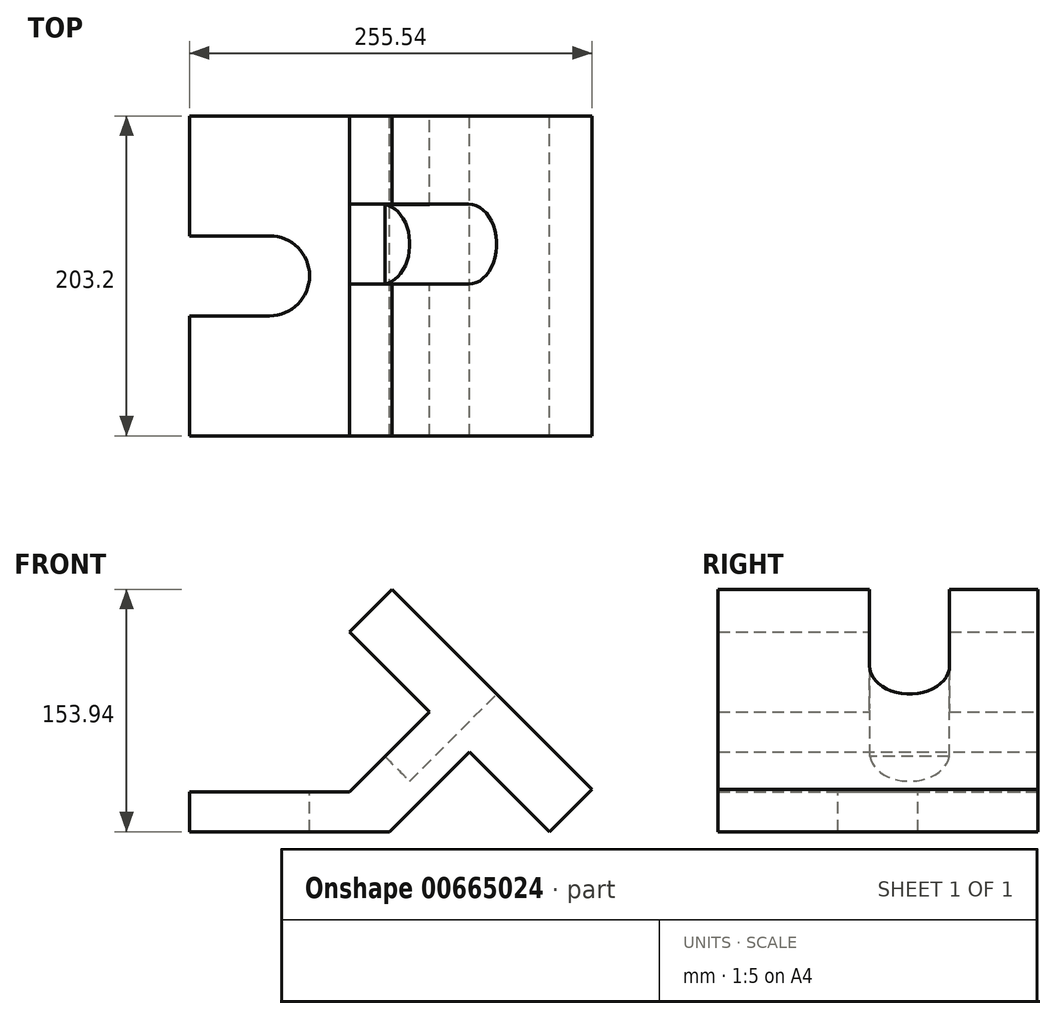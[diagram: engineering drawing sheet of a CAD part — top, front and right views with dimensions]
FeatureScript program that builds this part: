
annotation { "Feature Type Name" : "Feature", "Feature Type Description" : "" }
export const myFeature = defineFeature(function(context is Context, id is Id, definition is map)
    precondition{}
    {
        {
            var Q0;
            Q0=qCreatedBy(makeId("Front.planeOp"),FACE);
            var sketch = newSketch(context, id + "F0", { "sketchPlane" : qUnion([Q0])});
            skLineSegment(sketch, "E0", {"start": v(0, 0) * mm, "end": v(127, 0) * mm});
            skLineSegment(sketch, "E1", {"start": v(0, 0) * mm, "end": v(0, 25.4) * mm});
            skLineSegment(sketch, "E2", {"start": v(0, 25.4) * mm, "end": v(101.6, 25.4) * mm});
            skLineSegment(sketch, "E3", {"start": v(152.4, 76.2) * mm, "end": v(101.6, 127) * mm});
            skLineSegment(sketch, "E4", {"start": v(152.4, 76.2) * mm, "end": v(101.6, 25.4) * mm});
            skLineSegment(sketch, "E5.0", {"start": v(179.34, 103.14) * mm, "end": v(128.54, 153.94) * mm});
            skLineSegment(sketch, "E6", {"start": v(101.6, 127) * mm, "end": v(128.54, 153.94) * mm});
            skLineSegment(sketch, "E7", {"start": v(177.8, 50.8) * mm, "end": v(127, 0) * mm});
            skLineSegment(sketch, "E8", {"start": v(228.6, 0) * mm, "end": v(177.8, 50.8) * mm});
            skLineSegment(sketch, "E9.0", {"start": v(255.54, 26.94) * mm, "end": v(204.74, 77.74) * mm});
            skLineSegment(sketch, "E10", {"start": v(179.34, 103.14) * mm, "end": v(204.74, 77.74) * mm});
            skLineSegment(sketch, "E11", {"start": v(255.54, 26.94) * mm, "end": v(228.6, 0) * mm});
            skSolve(sketch);
        }
        {
            var Q0;
            Q0=makeQuery(id+"F0.imprint","IMPRINT",FACE,{"disambiguationData":[TD([[makeQuery(id+"F0.imprint","IMPRINT",EDGE,{"derivedFrom":sQuery(id+"F0.wireOp",EDGE,"E0")}),1.0]])]});
            extrude(context, id + "F1", {"entities" : qUnion([Q0]), "endBound" : BoundingType.SYMMETRIC, "depth" : 203.2 * mm, "offsetDistance" : 25.4 * mm});
        }
        {
            var Q0;
            Q0=makeQuery(id+"F1.opExtrude","SWEPT_FACE",FACE,{"disambiguationData":[OSD([sQuery(id+"F0.wireOp",EDGE,"E5.0"),sQuery(id+"F0.wireOp",EDGE,"E9.0"),sQuery(id+"F0.wireOp",EDGE,"E10")])]});
            var sketch = newSketch(context, id + "F2", { "sketchPlane" : qUnion([Q0])});
            skArc(sketch, "E12", {"start": v(-5.26, -50.8) * mm, "mid": v(20.14, -76.2) * mm, "end": v(45.54, -50.8) * mm});
            skArc(sketch, "E13", {"start": v(45.54, 50.8) * mm, "mid": v(20.14, 76.2) * mm, "end": v(-5.26, 50.8) * mm});
            skArc(sketch, "E14", {"start": v(96.34, -50.8) * mm, "mid": v(121.87, -76.2) * mm, "end": v(147.14, -50.54) * mm});
            skArc(sketch, "E15", {"start": v(147.14, 50.54) * mm, "mid": v(121.87, 76.2) * mm, "end": v(96.34, 50.8) * mm});
            skLineSegment(sketch, "E16", {"start": v(-5.26, -50.8) * mm, "end": v(-5.26, 50.8) * mm});
            skLineSegment(sketch, "E17", {"start": v(45.54, -50.8) * mm, "end": v(45.54, 50.8) * mm});
            skLineSegment(sketch, "E18", {"start": v(96.34, 50.8) * mm, "end": v(96.34, -50.8) * mm});
            skLineSegment(sketch, "E19", {"start": v(147.14, -51.06) * mm, "end": v(147.14, 50.54) * mm});
            skSolve(sketch);
        }
        {
            var Q0;
            Q0=makeQuery(id+"F2.imprint","IMPRINT",FACE,{"disambiguationData":[TD([[makeQuery(id+"F2.imprint","IMPRINT",EDGE,{"derivedFrom":sQuery(id+"F2.wireOp",EDGE,"E12")}),1.0]])]});
            var Q1;
            {var subQ4=sQuery(id+"F2.wireOp",EDGE,"E15");Q1=makeQuery(id+"F2.imprint","IMPRINT",FACE,{"disambiguationData":[TD([[makeQuery(id+"F2.imprint","IMPRINT",EDGE,{"derivedFrom":subQ4}),1.0]])]});}
            extrude(context, id + "F3", {"entities" : qUnion([Q0, Q1]), "operationType" : NewBodyOperationType.REMOVE, "oppositeDirection" : true, "depth" : 78.23 * mm, "offsetDistance" : 25.4 * mm});
        }
        {
            var Q0;
            Q0=makeQuery(id+"F1.opExtrude","SWEPT_FACE",FACE,{"disambiguationData":[OSD([sQuery(id+"F0.wireOp",EDGE,"E2")])]});
            var sketch = newSketch(context, id + "F4", { "sketchPlane" : qUnion([Q0])});
            skLineSegment(sketch, "E20", {"start": v(0, 101.6) * mm, "end": v(0, 25.4) * mm});
            skLineSegment(sketch, "E21", {"start": v(0, -101.6) * mm, "end": v(0, -25.4) * mm});
            skLineSegment(sketch, "E22", {"start": v(0, -25.4) * mm, "end": v(50.8, -25.4) * mm});
            skLineSegment(sketch, "E23", {"start": v(50.8, 25.4) * mm, "end": v(0, 25.4) * mm});
            skArc(sketch, "E24", {"start": v(50.8, -25.4) * mm, "mid": v(76.2, 0) * mm, "end": v(50.8, 25.4) * mm});
            skSolve(sketch);
        }
        {
            var Q0;
            {var subQ0=sQuery(id+"F4.wireOp",EDGE,"E22");Q0=makeQuery(id+"F4.imprint","IMPRINT",FACE,{"disambiguationData":[TD([[makeQuery(id+"F4.imprint","IMPRINT",EDGE,{"derivedFrom":subQ0}),1.0]])]});}
            extrude(context, id + "F5", {"entities" : qUnion([Q0]), "operationType" : NewBodyOperationType.REMOVE, "oppositeDirection" : true, "depth" : 32.5 * mm, "offsetDistance" : 25.4 * mm});
        }
    });
